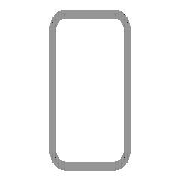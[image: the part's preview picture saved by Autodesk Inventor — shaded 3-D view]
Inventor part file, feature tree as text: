
AUTODESK INVENTOR PART (.ipt)
format: ipt  version: 2025 (Build 290162010, 162A)  size: 136,192 bytes
history: native  units: mm (DEFAULTED — no unit token found)
features: other x4, sketch x1, plane x1
ambient origin geometry x8: Origin, YZ Plane, XZ Plane, XY Plane, X Axis, Y Axis, Z Axis, Center Point
bodies: Solid1 (feature_tree), Body (feature_tree)
feature tree (6):
  parser-record x1  (decoder bookkeeping rows leaked as tree rows — omitted from the tree; the rows remain in map.json)
  other  "Driven Length"
  other  "Start Plane"
  other  "End Plane"
  sketch  "Sketch3"  dims[d3=300.0mm d4=0.0mm d7=3.75mm d10=60.0mm d11=40.0mm d12=2.5mm d13=-0.0mm d14=300.0mm d15=30.0mm d16=20.0mm d17=90.0deg d18=300.0mm]
  plane  "Work Plane3"
